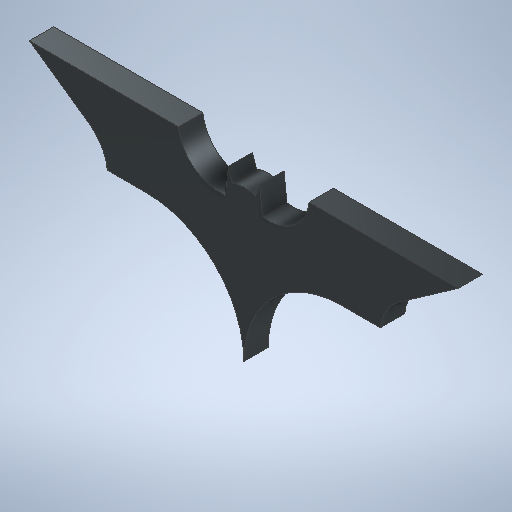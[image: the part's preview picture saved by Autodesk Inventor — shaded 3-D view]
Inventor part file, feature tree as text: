
AUTODESK INVENTOR PART (.ipt)
format: ipt  version: 2025.2 (Build 292293000, 293)  size: 308,224 bytes
history: native  units: mm
features: extrude x1, sketch x1
ambient origin geometry x8: Origin, YZ Plane, XZ Plane, XY Plane, X Axis, Y Axis, Z Axis, Center Point
bodies: Solid1 (feature_tree)
feature tree (2):
  extrude  "Extrusion1"  Depth=25.0mm
  sketch  "Sketch1"  dims[d1=67.0mm d2=220.0mm d3=6.108652mm d4=45.0mm d5=140.0mm d6=100.0mm d7=75.0mm d8=100.0mm d9=100.0mm d10=30.0mm d11=50.0mm d12=12.0mm d13=10.0mm d14=37.0mm d15=4.363323mm d21=42.0mm d23=14.660766mm d24=25.0mm d25=0.0mm]
